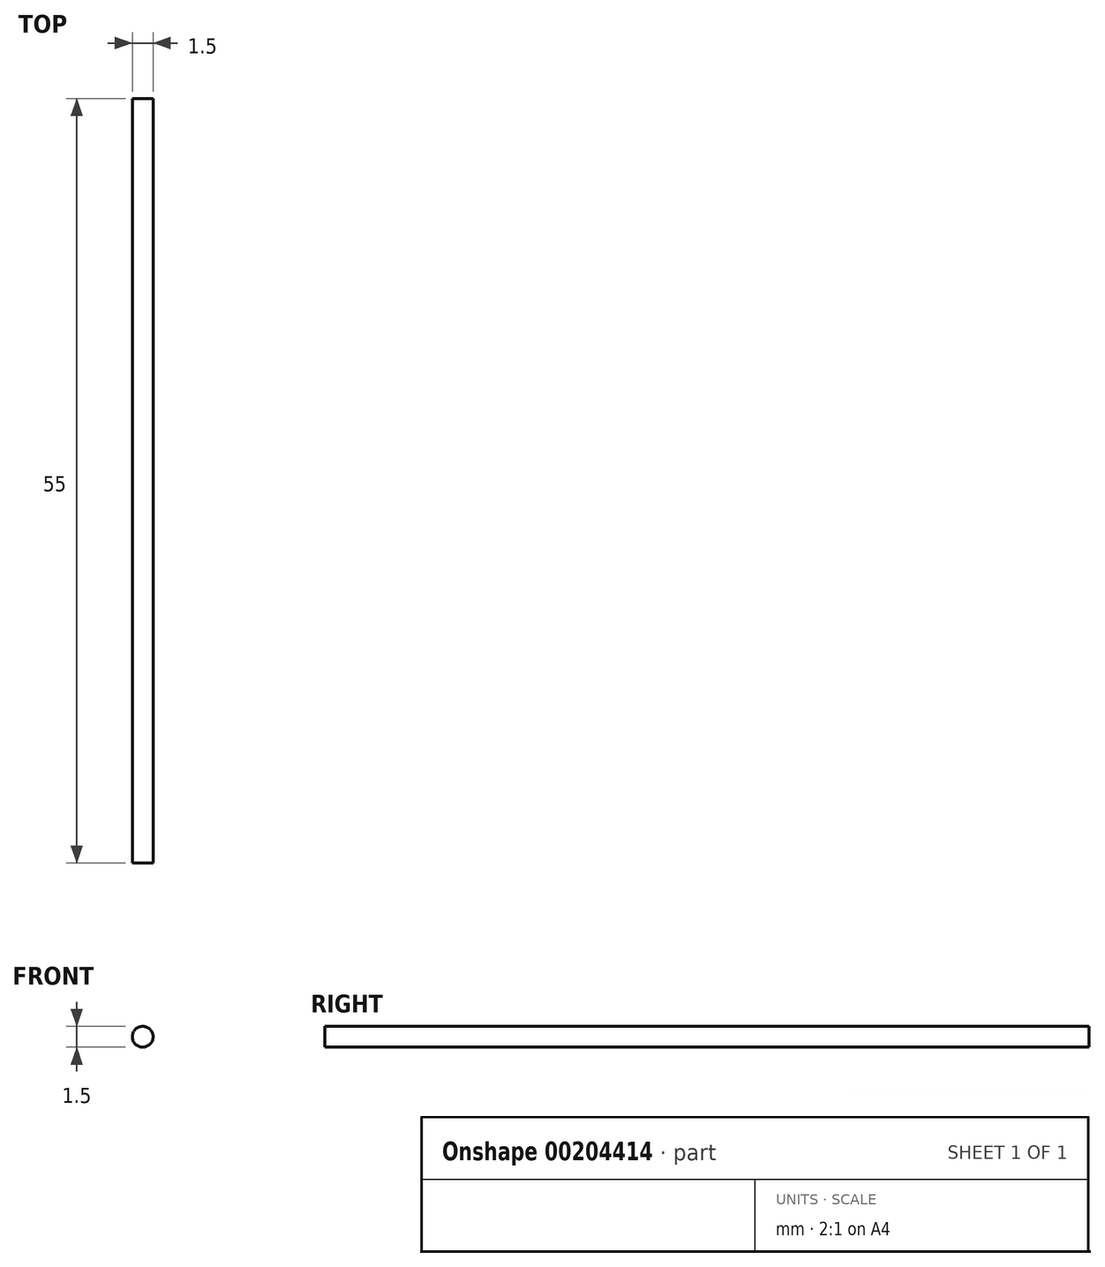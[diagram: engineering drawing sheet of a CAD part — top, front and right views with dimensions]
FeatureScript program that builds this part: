
annotation { "Feature Type Name" : "Feature", "Feature Type Description" : "" }
export const myFeature = defineFeature(function(context is Context, id is Id, definition is map)
    precondition{}
    {
        {
            var Q0;
            Q0=qCreatedBy(makeId("Front.planeOp"),FACE);
            var sketch = newSketch(context, id + "F0", { "sketchPlane" : qUnion([Q0])});
            skCircle(sketch, "E0", {"center": v(0, 0) * mm, "radius": 0.75 * mm});
            skSolve(sketch);
        }
        {
            var Q0;
            Q0 = qSketchRegion(id + "F0", true);
            extrude(context, id + "F1", {"entities" : qUnion([Q0]), "depth" : 55 * mm});
        }
    });
